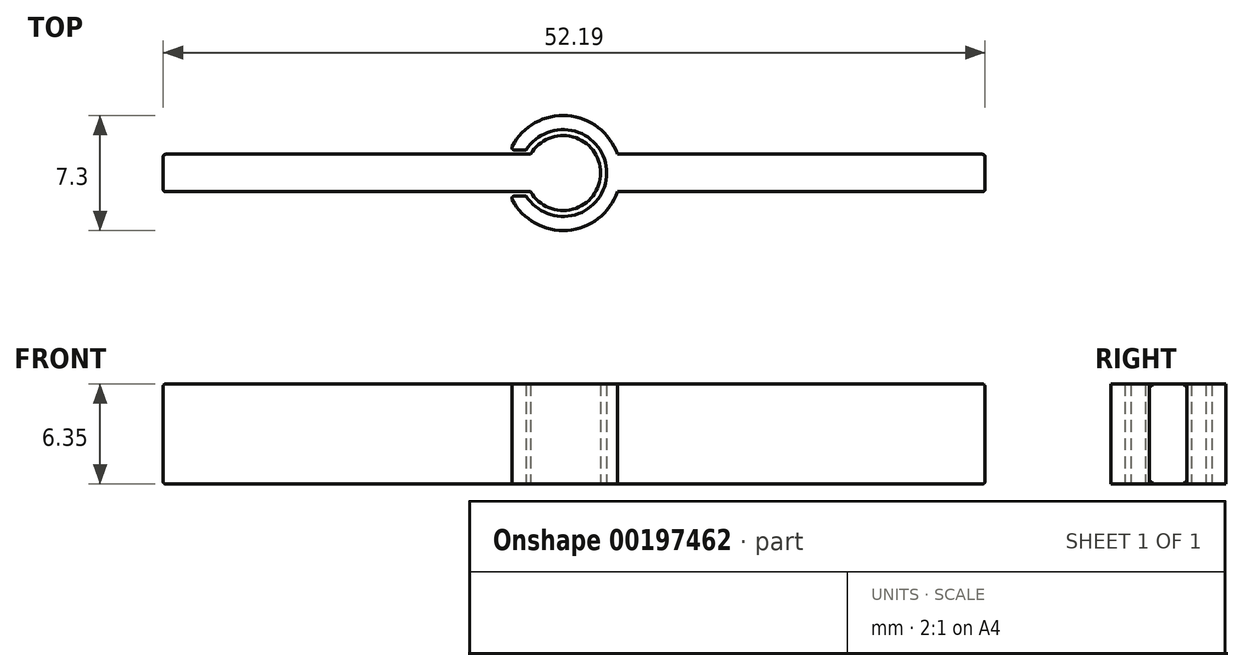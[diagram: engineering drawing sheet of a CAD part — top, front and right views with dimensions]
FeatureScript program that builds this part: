
annotation { "Feature Type Name" : "Feature", "Feature Type Description" : "" }
export const myFeature = defineFeature(function(context is Context, id is Id, definition is map)
    precondition{}
    {
        {
            var Q0;
            Q0=qCreatedBy(makeId("Top.planeOp"),FACE);
            var sketch = newSketch(context, id + "F0", { "sketchPlane" : qUnion([Q0])});
            skLineSegment(sketch, "E0.bottom", {"start": v(0, 1.2) * mm, "end": v(-2.06, 1.2) * mm, "construction": true});
            skLineSegment(sketch, "E0.top", {"start": v(0, -1.2) * mm, "end": v(-2.06, -1.2) * mm, "construction": true});
            skLineSegment(sketch, "E0.left", {"start": v(0, 1.2) * mm, "end": v(0, -1.2) * mm, "construction": true});
            skLineSegment(sketch, "E0.right", {"start": v(-25.4, 1.2) * mm, "end": v(-25.4, -1.2) * mm});
            skLineSegment(sketch, "E1", {"start": v(-2.06, 1.2) * mm, "end": v(-25.4, 1.2) * mm});
            skLineSegment(sketch, "E2", {"start": v(-2.06, -1.2) * mm, "end": v(-25.4, -1.2) * mm});
            skArc(sketch, "E3", {"start": v(-2.06, 1.2) * mm, "mid": v(-2.38, 0) * mm, "end": v(-2.06, -1.2) * mm, "construction": true});
            skArc(sketch, "E4", {"start": v(-2.06, -1.2) * mm, "mid": v(2.38, 0) * mm, "end": v(-2.06, 1.2) * mm});
            skLineSegment(sketch, "E5.0", {"start": v(-2.27, 1.57) * mm, "end": v(-3.3, 1.57) * mm, "construction": true});
            skArc(sketch, "E5.1", {"start": v(-2.27, -1.57) * mm, "mid": v(2.3, 1.52) * mm, "end": v(-2.34, -1.46) * mm, "construction": true});
            skLineSegment(sketch, "E5.2", {"start": v(-2.27, -1.57) * mm, "end": v(-3.3, -1.57) * mm, "construction": true});
            skArc(sketch, "E6", {"start": v(-3.3, 1.57) * mm, "mid": v(-3.65, 0) * mm, "end": v(-3.3, -1.57) * mm, "construction": true});
            skArc(sketch, "E7", {"start": v(-3.3, -1.57) * mm, "mid": v(3.32, 1.52) * mm, "end": v(-3.35, -1.46) * mm, "construction": true});
            skLineSegment(sketch, "E8.bottom", {"start": v(0, 1.2) * mm, "end": v(3.45, 1.2) * mm, "construction": true});
            skLineSegment(sketch, "E8.top", {"start": v(0, -1.2) * mm, "end": v(3.45, -1.2) * mm, "construction": true});
            skLineSegment(sketch, "E8.right", {"start": v(26.79, 1.2) * mm, "end": v(26.79, -1.2) * mm});
            skLineSegment(sketch, "E9", {"start": v(3.45, 1.2) * mm, "end": v(26.79, 1.2) * mm});
            skLineSegment(sketch, "E10", {"start": v(3.45, -1.2) * mm, "end": v(26.79, -1.2) * mm});
            skArc(sketch, "E11", {"start": v(3.45, 1.2) * mm, "mid": v(0.14, 3.65) * mm, "end": v(-3.35, 1.46) * mm});
            skArc(sketch, "E12", {"start": v(3.45, -1.2) * mm, "mid": v(3.65, 0) * mm, "end": v(3.45, 1.2) * mm, "construction": true});
            skLineSegment(sketch, "E13", {"start": v(-3.35, -1.46) * mm, "end": v(-2.34, -1.46) * mm});
            skLineSegment(sketch, "E14", {"start": v(-3.35, 1.46) * mm, "end": v(-2.34, 1.46) * mm});
            skArc(sketch, "E15", {"start": v(-3.35, 1.46) * mm, "mid": v(3.32, -1.52) * mm, "end": v(-3.3, 1.57) * mm, "construction": true});
            skArc(sketch, "E16", {"start": v(-2.34, 1.46) * mm, "mid": v(2.3, -1.52) * mm, "end": v(-2.27, 1.57) * mm, "construction": true});
            skArc(sketch, "E17", {"start": v(-2.34, -1.46) * mm, "mid": v(2.76, 0) * mm, "end": v(-2.34, 1.46) * mm});
            skArc(sketch, "E18", {"start": v(-3.35, -1.46) * mm, "mid": v(0.14, -3.65) * mm, "end": v(3.45, -1.2) * mm});
            skSolve(sketch);
        }
        {
            var Q0;
            Q0 = qSketchRegion(id + "F0", true);
            extrude(context, id + "F1", {"entities" : qUnion([Q0]), "depth" : 6.35 * mm});
        }
        {
            var Q0;
            Q0=makeQuery(id+"F1.opExtrude","SWEPT_EDGE",EDGE,{"disambiguationData":[OSD([sQuery(id+"F0.wireOp",EDGE,"E11"),sQuery(id+"F0.wireOp",EDGE,"E14")])]});
            var Q1;
            Q1=makeQuery(id+"F1.opExtrude","SWEPT_EDGE",EDGE,{"disambiguationData":[OSD([sQuery(id+"F0.wireOp",EDGE,"E13"),sQuery(id+"F0.wireOp",EDGE,"E18")])]});
            fillet(context, id + "F2", {"entities" : qUnion([Q0, Q1]), "radius" : 0.16 * mm, "tangentPropagation" : true, "allowEdgeOverflow" : false});
        }
        {
            var Q0;
            Q0=makeQuery(id+"F1.opExtrude","SWEPT_FACE",FACE,{"disambiguationData":[OSD([sQuery(id+"F0.wireOp",EDGE,"E0.right")])]});
            var Q1;
            Q1=makeQuery(id+"F1.opExtrude","SWEPT_FACE",FACE,{"disambiguationData":[OSD([sQuery(id+"F0.wireOp",EDGE,"E8.right")])]});
            fillet(context, id + "F3", {"entities" : qUnion([Q0, Q1]), "radius" : 0.15 * mm, "tangentPropagation" : true, "allowEdgeOverflow" : false});
        }
    });
